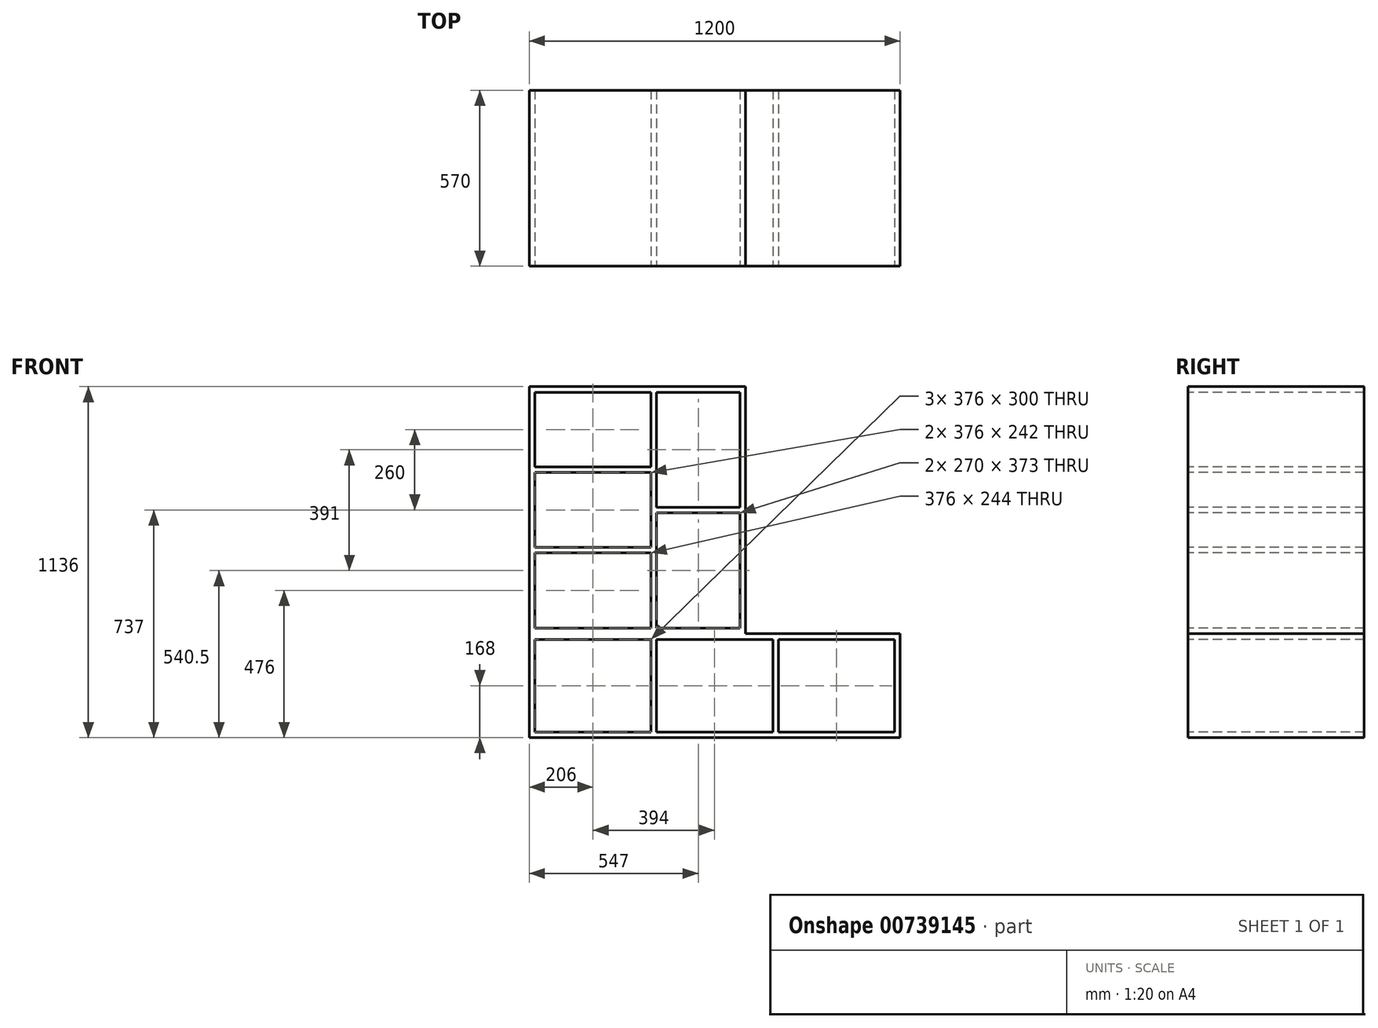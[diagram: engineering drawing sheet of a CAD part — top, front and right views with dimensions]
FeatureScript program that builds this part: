
annotation { "Feature Type Name" : "Feature", "Feature Type Description" : "" }
export const myFeature = defineFeature(function(context is Context, id is Id, definition is map)
    precondition{}
    {
        {
            var Q0;
            Q0=qCreatedBy(makeId("Top.planeOp"),FACE);
            var sketch = newSketch(context, id + "F0", { "sketchPlane" : qUnion([Q0])});
            skLineSegment(sketch, "E0.bottom", {"start": v(600, -285) * mm, "end": v(-600, -285) * mm});
            skLineSegment(sketch, "E0.top", {"start": v(600, 285) * mm, "end": v(-600, 285) * mm});
            skLineSegment(sketch, "E0.left", {"start": v(600, -285) * mm, "end": v(600, 285) * mm});
            skLineSegment(sketch, "E0.right", {"start": v(-600, -285) * mm, "end": v(-600, 285) * mm});
            skPoint(sketch, "E0.middle", {"position": v(0, 0) * mm});
            skSolve(sketch);
        }
        {
            var Q0;
            Q0=makeQuery(id+"F0.imprint","IMPRINT",FACE,{"disambiguationData":[TD([[makeQuery(id+"F0.imprint","IMPRINT",EDGE,{"derivedFrom":sQuery(id+"F0.wireOp",EDGE,"E0.bottom")}),-1.0]])]});
            extrude(context, id + "F1", {"entities" : qUnion([Q0]), "depth" : 18 * mm, "offsetDistance" : 25 * mm});
        }
        {
            var Q0;
            Q0=makeQuery(id+"F1.opExtrude","CAP_FACE",FACE,{"disambiguationData":[OSD([sQuery(id+"F0.wireOp",EDGE,"E0.bottom"),sQuery(id+"F0.wireOp",EDGE,"E0.top"),sQuery(id+"F0.wireOp",EDGE,"E0.left"),sQuery(id+"F0.wireOp",EDGE,"E0.right")])],"isStart":false});
            var sketch = newSketch(context, id + "F2", { "sketchPlane" : qUnion([Q0])});
            skLineSegment(sketch, "E1.bottom", {"start": v(-600, 285) * mm, "end": v(-582, 285) * mm});
            skLineSegment(sketch, "E1.top", {"start": v(-600, -285) * mm, "end": v(-582, -285) * mm});
            skLineSegment(sketch, "E1.left", {"start": v(-600, 285) * mm, "end": v(-600, -285) * mm});
            skLineSegment(sketch, "E1.right", {"start": v(-582, 285) * mm, "end": v(-582, -285) * mm});
            skLineSegment(sketch, "E2.bottom", {"start": v(-206, 285) * mm, "end": v(-188, 285) * mm});
            skLineSegment(sketch, "E2.top", {"start": v(-206, -285) * mm, "end": v(-188, -285) * mm});
            skLineSegment(sketch, "E2.left", {"start": v(-206, 285) * mm, "end": v(-206, -285) * mm});
            skLineSegment(sketch, "E2.right", {"start": v(-188, 285) * mm, "end": v(-188, -285) * mm});
            skLineSegment(sketch, "E3.bottom", {"start": v(188, 285) * mm, "end": v(206, 285) * mm});
            skLineSegment(sketch, "E3.top", {"start": v(188, -285) * mm, "end": v(206, -285) * mm});
            skLineSegment(sketch, "E3.left", {"start": v(188, 285) * mm, "end": v(188, -285) * mm});
            skLineSegment(sketch, "E3.right", {"start": v(206, 285) * mm, "end": v(206, -285) * mm});
            skLineSegment(sketch, "E4.bottom", {"start": v(582, 285) * mm, "end": v(600, 285) * mm});
            skLineSegment(sketch, "E4.top", {"start": v(582, -285) * mm, "end": v(600, -285) * mm});
            skLineSegment(sketch, "E4.left", {"start": v(582, 285) * mm, "end": v(582, -285) * mm});
            skLineSegment(sketch, "E4.right", {"start": v(600, 285) * mm, "end": v(600, -285) * mm});
            skLineSegment(sketch, "E5.bottom", {"start": v(-582, 285) * mm, "end": v(-206, 285) * mm});
            skLineSegment(sketch, "E5.top", {"start": v(-582, 92.44) * mm, "end": v(-206, 92.44) * mm});
            skLineSegment(sketch, "E5.left", {"start": v(-582, 285) * mm, "end": v(-582, 92.44) * mm});
            skLineSegment(sketch, "E5.right", {"start": v(-206, 285) * mm, "end": v(-206, 92.44) * mm});
            skLineSegment(sketch, "E6.bottom", {"start": v(-188, 285) * mm, "end": v(188, 285) * mm});
            skLineSegment(sketch, "E6.top", {"start": v(-188, 93.68) * mm, "end": v(188, 93.68) * mm});
            skLineSegment(sketch, "E6.left", {"start": v(-188, 285) * mm, "end": v(-188, 93.68) * mm});
            skLineSegment(sketch, "E6.right", {"start": v(188, 285) * mm, "end": v(188, 93.68) * mm});
            skLineSegment(sketch, "E7.bottom", {"start": v(206, 285) * mm, "end": v(582, 285) * mm});
            skLineSegment(sketch, "E7.top", {"start": v(206, 93.68) * mm, "end": v(582, 93.68) * mm});
            skLineSegment(sketch, "E7.left", {"start": v(206, 285) * mm, "end": v(206, 93.68) * mm});
            skLineSegment(sketch, "E7.right", {"start": v(582, 285) * mm, "end": v(582, 93.68) * mm});
            skSolve(sketch);
        }
        {
            var Q0;
            Q0=makeQuery(id+"F2.imprint","IMPRINT",FACE,{"disambiguationData":[TD([[makeQuery(id+"F2.imprint","IMPRINT",EDGE,{"derivedFrom":sQuery(id+"F2.wireOp",EDGE,"E1.bottom")}),1.0]])]});
            var Q1;
            Q1=makeQuery(id+"F2.imprint","IMPRINT",FACE,{"disambiguationData":[TD([[makeQuery(id+"F2.imprint","IMPRINT",EDGE,{"derivedFrom":sQuery(id+"F2.wireOp",EDGE,"E2.bottom")}),1.0]])]});
            var Q2;
            Q2=makeQuery(id+"F2.imprint","IMPRINT",FACE,{"disambiguationData":[TD([[makeQuery(id+"F2.imprint","IMPRINT",EDGE,{"derivedFrom":sQuery(id+"F2.wireOp",EDGE,"E3.bottom")}),1.0]])]});
            var Q3;
            Q3=makeQuery(id+"F2.imprint","IMPRINT",FACE,{"disambiguationData":[TD([[makeQuery(id+"F2.imprint","IMPRINT",EDGE,{"derivedFrom":sQuery(id+"F2.wireOp",EDGE,"E4.bottom")}),1.0]])]});
            extrude(context, id + "F3", {"entities" : qUnion([Q0, Q1, Q2, Q3]), "operationType" : NewBodyOperationType.ADD, "depth" : 300 * mm, "offsetDistance" : 25 * mm});
        }
        {
            var Q0;
            Q0=makeQuery(id+"F3.opExtrude","CAP_FACE",FACE,{"disambiguationData":[OSD([sQuery(id+"F2.wireOp",EDGE,"E3.bottom"),sQuery(id+"F2.wireOp",EDGE,"E3.top"),sQuery(id+"F2.wireOp",EDGE,"E3.left"),sQuery(id+"F2.wireOp",EDGE,"E3.right")])],"isStart":false});
            var sketch = newSketch(context, id + "F4", { "sketchPlane" : qUnion([Q0])});
            skLineSegment(sketch, "E8.bottom", {"start": v(600, -285) * mm, "end": v(-600, -285) * mm});
            skLineSegment(sketch, "E8.top", {"start": v(600, 285) * mm, "end": v(-600, 285) * mm});
            skLineSegment(sketch, "E8.left", {"start": v(600, -285) * mm, "end": v(600, 285) * mm});
            skLineSegment(sketch, "E8.right", {"start": v(-600, -285) * mm, "end": v(-600, 285) * mm});
            skPoint(sketch, "E8.middle", {"position": v(0, 0) * mm});
            skSolve(sketch);
        }
        {
            var Q0;
            Q0 = qSketchRegion(id + "F4", true);
            extrude(context, id + "F5", {"entities" : qUnion([Q0]), "operationType" : NewBodyOperationType.ADD, "depth" : 18 * mm, "offsetDistance" : 25 * mm});
        }
        {
            var Q0;
            Q0=makeQuery(id+"F5.opExtrude","CAP_FACE",FACE,{"disambiguationData":[OSD([sQuery(id+"F4.wireOp",EDGE,"E8.bottom"),sQuery(id+"F4.wireOp",EDGE,"E8.top"),sQuery(id+"F4.wireOp",EDGE,"E8.left"),sQuery(id+"F4.wireOp",EDGE,"E8.right")])],"isStart":false});
            var sketch = newSketch(context, id + "F6", { "sketchPlane" : qUnion([Q0])});
            skLineSegment(sketch, "E9.bottom", {"start": v(-600, 285) * mm, "end": v(100, 285) * mm});
            skLineSegment(sketch, "E9.top", {"start": v(-600, -285) * mm, "end": v(100, -285) * mm});
            skLineSegment(sketch, "E9.left", {"start": v(-600, 285) * mm, "end": v(-600, -285) * mm});
            skLineSegment(sketch, "E9.right", {"start": v(100, 285) * mm, "end": v(100, -285) * mm});
            skSolve(sketch);
        }
        {
            var Q0;
            Q0=makeQuery(id+"F6.imprint","IMPRINT",FACE,{"disambiguationData":[TD([[makeQuery(id+"F6.imprint","IMPRINT",EDGE,{"derivedFrom":sQuery(id+"F6.wireOp",EDGE,"E9.bottom")}),1.0]])]});
            extrude(context, id + "F7", {"entities" : qUnion([Q0]), "operationType" : NewBodyOperationType.ADD, "depth" : 18 * mm, "offsetDistance" : 25 * mm});
        }
        {
            var Q0;
            Q0=makeQuery(id+"F7.opExtrude","CAP_FACE",FACE,{"disambiguationData":[OSD([sQuery(id+"F6.wireOp",EDGE,"E9.bottom"),sQuery(id+"F6.wireOp",EDGE,"E9.top"),sQuery(id+"F6.wireOp",EDGE,"E9.left"),sQuery(id+"F6.wireOp",EDGE,"E9.right")])],"isStart":false});
            var sketch = newSketch(context, id + "F8", { "sketchPlane" : qUnion([Q0])});
            skLineSegment(sketch, "E10.bottom", {"start": v(-600, 285) * mm, "end": v(-582, 285) * mm});
            skLineSegment(sketch, "E10.top", {"start": v(-600, -285) * mm, "end": v(-582, -285) * mm});
            skLineSegment(sketch, "E10.left", {"start": v(-600, 285) * mm, "end": v(-600, -285) * mm});
            skLineSegment(sketch, "E10.right", {"start": v(-582, 285) * mm, "end": v(-582, -285) * mm});
            skLineSegment(sketch, "E11.bottom", {"start": v(82, 285) * mm, "end": v(100, 285) * mm});
            skLineSegment(sketch, "E11.top", {"start": v(82, -285) * mm, "end": v(100, -285) * mm});
            skLineSegment(sketch, "E11.left", {"start": v(82, 285) * mm, "end": v(82, -285) * mm});
            skLineSegment(sketch, "E11.right", {"start": v(100, 285) * mm, "end": v(100, -285) * mm});
            skSolve(sketch);
        }
        {
            var Q0;
            Q0=makeQuery(id+"F8.imprint","IMPRINT",FACE,{"disambiguationData":[TD([[makeQuery(id+"F8.imprint","IMPRINT",EDGE,{"derivedFrom":sQuery(id+"F8.wireOp",EDGE,"E10.bottom")}),1.0]])]});
            var Q1;
            Q1=makeQuery(id+"F8.imprint","IMPRINT",FACE,{"disambiguationData":[TD([[makeQuery(id+"F8.imprint","IMPRINT",EDGE,{"derivedFrom":sQuery(id+"F8.wireOp",EDGE,"E11.bottom")}),1.0]])]});
            extrude(context, id + "F9", {"entities" : qUnion([Q0, Q1]), "operationType" : NewBodyOperationType.ADD, "depth" : 764 * mm, "offsetDistance" : 25 * mm});
        }
        {
            var Q0;
            Q0=makeQuery(id+"F9.opExtrude","CAP_FACE",FACE,{"disambiguationData":[OSD([sQuery(id+"F8.wireOp",EDGE,"E11.bottom"),sQuery(id+"F8.wireOp",EDGE,"E11.top"),sQuery(id+"F8.wireOp",EDGE,"E11.left"),sQuery(id+"F8.wireOp",EDGE,"E11.right")])],"isStart":false});
            var sketch = newSketch(context, id + "F10", { "sketchPlane" : qUnion([Q0])});
            skLineSegment(sketch, "E12.bottom", {"start": v(100, -285) * mm, "end": v(-600, -285) * mm});
            skLineSegment(sketch, "E12.top", {"start": v(100, 285) * mm, "end": v(-600, 285) * mm});
            skLineSegment(sketch, "E12.left", {"start": v(100, -285) * mm, "end": v(100, 285) * mm});
            skLineSegment(sketch, "E12.right", {"start": v(-600, -285) * mm, "end": v(-600, 285) * mm});
            skSolve(sketch);
        }
        {
            var Q0;
            {var subQ2=sQuery(id+"F10.wireOp",EDGE,"E12.right");Q0=makeQuery(id+"F10.imprint","IMPRINT",FACE,{"disambiguationData":[TD([[makeQuery(id+"F10.imprint","IMPRINT",EDGE,{"derivedFrom":subQ2}),-1.0]])]});}
            var Q1;
            {var subQ0=sQuery(id+"F10.wireOp",EDGE,"E12.left");Q1=makeQuery(id+"F10.imprint","IMPRINT",FACE,{"disambiguationData":[TD([[makeQuery(id+"F10.imprint","IMPRINT",EDGE,{"derivedFrom":subQ0}),-1.0]])]});}
            extrude(context, id + "F11", {"entities" : qUnion([Q0, Q1]), "operationType" : NewBodyOperationType.ADD, "depth" : 18 * mm, "offsetDistance" : 25 * mm});
        }
        {
            var Q0;
            Q0=makeQuery(id+"F7.opExtrude","CAP_FACE",FACE,{"disambiguationData":[OSD([sQuery(id+"F6.wireOp",EDGE,"E9.bottom"),sQuery(id+"F6.wireOp",EDGE,"E9.top"),sQuery(id+"F6.wireOp",EDGE,"E9.left"),sQuery(id+"F6.wireOp",EDGE,"E9.right")])],"isStart":false});
            var sketch = newSketch(context, id + "F12", { "sketchPlane" : qUnion([Q0])});
            skLineSegment(sketch, "E13.bottom", {"start": v(-582, 285) * mm, "end": v(-206, 285) * mm});
            skLineSegment(sketch, "E13.top", {"start": v(-582, -285) * mm, "end": v(-206, -285) * mm});
            skLineSegment(sketch, "E13.left", {"start": v(-582, 285) * mm, "end": v(-582, -285) * mm});
            skLineSegment(sketch, "E13.right", {"start": v(-206, 285) * mm, "end": v(-206, -285) * mm});
            skLineSegment(sketch, "E14.bottom", {"start": v(-206, 285) * mm, "end": v(-188, 285) * mm});
            skLineSegment(sketch, "E14.top", {"start": v(-206, -285) * mm, "end": v(-188, -285) * mm});
            skLineSegment(sketch, "E14.right", {"start": v(-188, 285) * mm, "end": v(-188, -285) * mm});
            skSolve(sketch);
        }
        {
            var Q0;
            Q0=makeQuery(id+"F12.imprint","IMPRINT",FACE,{"disambiguationData":[TD([[makeQuery(id+"F12.imprint","IMPRINT",EDGE,{"derivedFrom":sQuery(id+"F12.wireOp",EDGE,"E14.bottom")}),1.0]])]});
            extrude(context, id + "F13", {"entities" : qUnion([Q0]), "operationType" : NewBodyOperationType.ADD, "depth" : 764 * mm, "offsetDistance" : 25 * mm});
        }
        {
            var Q0;
            Q0=makeQuery(id+"FskYXZMth14vidH_1.boolean.opBoolean","MERGE",FACE,{"derivedFrom":[makeQuery(id+"F13.boolean.opBoolean","MERGE",FACE,{"derivedFrom":[makeQuery(id+"F11.boolean.opBoolean","MERGE",FACE,{"derivedFrom":[makeQuery(id+"F9.boolean.opBoolean","MERGE",FACE,{"derivedFrom":[makeQuery(id+"F7.boolean.opBoolean","MERGE",FACE,{"derivedFrom":[makeQuery(id+"F5.boolean.opBoolean","MERGE",FACE,{"derivedFrom":[makeQuery(id+"F3.boolean.opBoolean","MERGE",FACE,{"derivedFrom":[makeQuery(id+"F1.opExtrude","SWEPT_FACE",FACE,{"disambiguationData":[OSD([sQuery(id+"F0.wireOp",EDGE,"E0.bottom")])]}),makeQuery(id+"F3.opExtrude","SWEPT_FACE",FACE,{"disambiguationData":[OSD([sQuery(id+"F2.wireOp",EDGE,"E1.top")])]}),makeQuery(id+"F3.opExtrude","SWEPT_FACE",FACE,{"disambiguationData":[OSD([sQuery(id+"F2.wireOp",EDGE,"E2.top")])]}),makeQuery(id+"F3.opExtrude","SWEPT_FACE",FACE,{"disambiguationData":[OSD([sQuery(id+"F2.wireOp",EDGE,"E3.top")])]}),makeQuery(id+"F3.opExtrude","SWEPT_FACE",FACE,{"disambiguationData":[OSD([sQuery(id+"F2.wireOp",EDGE,"E4.top")])]})]}),makeQuery(id+"F5.opExtrude","SWEPT_FACE",FACE,{"disambiguationData":[OSD([sQuery(id+"F4.wireOp",EDGE,"E8.bottom")])]})]}),makeQuery(id+"F7.opExtrude","SWEPT_FACE",FACE,{"disambiguationData":[OSD([sQuery(id+"F6.wireOp",EDGE,"E9.top")])]})]}),makeQuery(id+"F9.opExtrude","SWEPT_FACE",FACE,{"disambiguationData":[OSD([sQuery(id+"F8.wireOp",EDGE,"E10.top")])]}),makeQuery(id+"F9.opExtrude","SWEPT_FACE",FACE,{"disambiguationData":[OSD([sQuery(id+"F8.wireOp",EDGE,"E11.top")])]})]}),makeQuery(id+"F11.opExtrude","SWEPT_FACE",FACE,{"disambiguationData":[OSD([sQuery(id+"F10.wireOp",EDGE,"E12.bottom")])]})]}),makeQuery(id+"F13.opExtrude","SWEPT_FACE",FACE,{"disambiguationData":[OSD([sQuery(id+"F12.wireOp",EDGE,"E14.top")])]})]}),makeQuery(id+"FskYXZMth14vidH_1.opExtrude","CAP_FACE",FACE,{"disambiguationData":[OSD([sQuery(id+"FjYDHQKFJiyF5Pm_1.wireOp",EDGE,"TK6zqZqr-b6AT-WknO-H30k-x74qHj6ZwECY.bottom"),sQuery(id+"FjYDHQKFJiyF5Pm_1.wireOp",EDGE,"TK6zqZqr-b6AT-WknO-H30k-x74qHj6ZwECY.top"),sQuery(id+"FjYDHQKFJiyF5Pm_1.wireOp",EDGE,"TK6zqZqr-b6AT-WknO-H30k-x74qHj6ZwECY.left"),sQuery(id+"FjYDHQKFJiyF5Pm_1.wireOp",EDGE,"TK6zqZqr-b6AT-WknO-H30k-x74qHj6ZwECY.right")])],"isStart":false})]});
            var sketch = newSketch(context, id + "F14", { "sketchPlane" : qUnion([Q0])});
            skLineSegment(sketch, "E15.bottom", {"start": v(-188, 1118) * mm, "end": v(82, 1118) * mm});
            skLineSegment(sketch, "E15.top", {"start": v(-188, 745) * mm, "end": v(82, 745) * mm});
            skLineSegment(sketch, "E15.left", {"start": v(-188, 1118) * mm, "end": v(-188, 745) * mm});
            skLineSegment(sketch, "E15.right", {"start": v(82, 1118) * mm, "end": v(82, 745) * mm});
            skLineSegment(sketch, "E16.top", {"start": v(-188, 727) * mm, "end": v(82, 727) * mm});
            skLineSegment(sketch, "E16.left", {"start": v(-188, 745) * mm, "end": v(-188, 727) * mm});
            skLineSegment(sketch, "E16.right", {"start": v(82, 745) * mm, "end": v(82, 727) * mm});
            skLineSegment(sketch, "E17.bottom", {"start": v(-582, 1118) * mm, "end": v(-206, 1118) * mm});
            skLineSegment(sketch, "E17.top", {"start": v(-582, 876) * mm, "end": v(-206, 876) * mm});
            skLineSegment(sketch, "E17.left", {"start": v(-582, 1118) * mm, "end": v(-582, 876) * mm});
            skLineSegment(sketch, "E17.right", {"start": v(-206, 1118) * mm, "end": v(-206, 876) * mm});
            skLineSegment(sketch, "E18.top", {"start": v(-582, 858) * mm, "end": v(-206, 858) * mm});
            skLineSegment(sketch, "E18.left", {"start": v(-582, 876) * mm, "end": v(-582, 858) * mm});
            skLineSegment(sketch, "E18.right", {"start": v(-206, 876) * mm, "end": v(-206, 858) * mm});
            skLineSegment(sketch, "E19.top", {"start": v(-582, 616) * mm, "end": v(-206, 616) * mm});
            skLineSegment(sketch, "E19.left", {"start": v(-582, 858) * mm, "end": v(-582, 616) * mm});
            skLineSegment(sketch, "E19.right", {"start": v(-206, 858) * mm, "end": v(-206, 616) * mm});
            skLineSegment(sketch, "E20.top", {"start": v(-582, 598) * mm, "end": v(-206, 598) * mm});
            skLineSegment(sketch, "E20.left", {"start": v(-582, 616) * mm, "end": v(-582, 598) * mm});
            skLineSegment(sketch, "E20.right", {"start": v(-206, 616) * mm, "end": v(-206, 598) * mm});
            skSolve(sketch);
        }
        {
            var Q0;
            Q0=makeQuery(id+"F14.imprint","IMPRINT",FACE,{"disambiguationData":[TD([[makeQuery(id+"F14.imprint","IMPRINT",EDGE,{"derivedFrom":sQuery(id+"F14.wireOp",EDGE,"E15.top")}),-1.0]])]});
            var Q1;
            Q1=makeQuery(id+"F14.imprint","IMPRINT",FACE,{"disambiguationData":[TD([[makeQuery(id+"F14.imprint","IMPRINT",EDGE,{"derivedFrom":sQuery(id+"F14.wireOp",EDGE,"E17.top")}),-1.0]])]});
            var Q2;
            Q2=makeQuery(id+"F14.imprint","IMPRINT",FACE,{"disambiguationData":[TD([[makeQuery(id+"F14.imprint","IMPRINT",EDGE,{"derivedFrom":sQuery(id+"F14.wireOp",EDGE,"E19.top")}),-1.0]])]});
            extrude(context, id + "F15", {"entities" : qUnion([Q0, Q1, Q2]), "operationType" : NewBodyOperationType.ADD, "oppositeDirection" : true, "depth" : 570 * mm, "offsetDistance" : 25 * mm});
        }
    });
